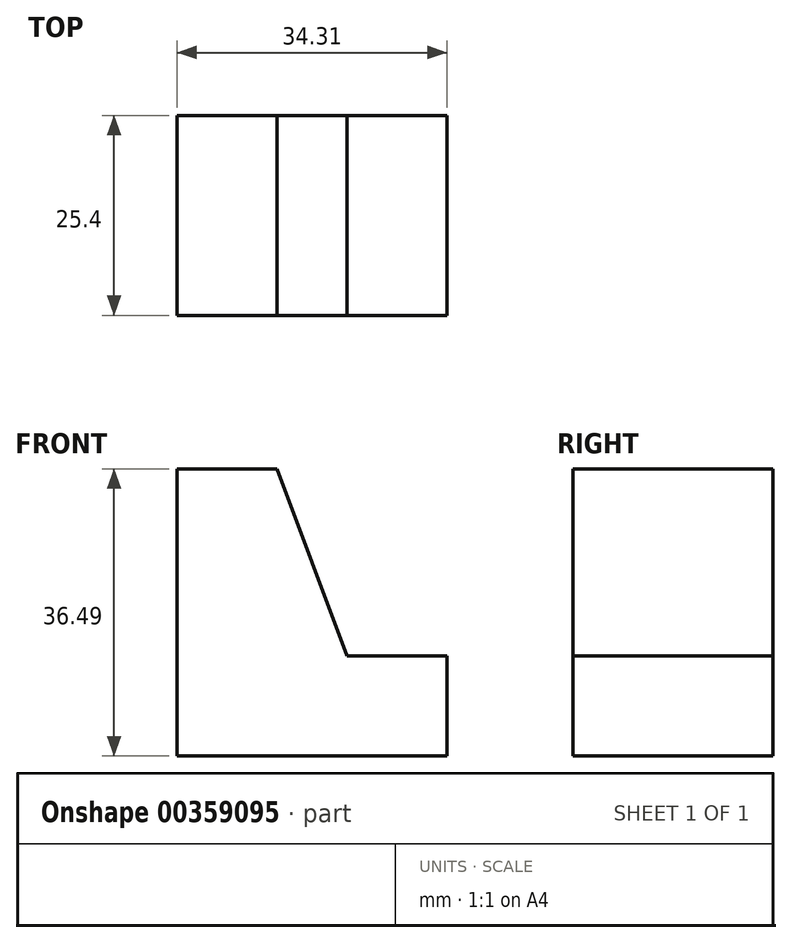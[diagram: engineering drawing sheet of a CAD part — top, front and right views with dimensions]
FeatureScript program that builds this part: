
annotation { "Feature Type Name" : "Feature", "Feature Type Description" : "" }
export const myFeature = defineFeature(function(context is Context, id is Id, definition is map)
    precondition{}
    {
        {
            var Q0;
            Q0=qCreatedBy(makeId("Front.planeOp"),FACE);
            var sketch = newSketch(context, id + "F0", { "sketchPlane" : qUnion([Q0])});
            skLineSegment(sketch, "E0", {"start": v(0, 0) * mm, "end": v(34.3, 0) * mm});
            skLineSegment(sketch, "E1", {"start": v(34.3, 0) * mm, "end": v(34.3, 12.7) * mm});
            skLineSegment(sketch, "E2", {"start": v(12.7, 36.49) * mm, "end": v(0, 36.49) * mm});
            skLineSegment(sketch, "E3", {"start": v(0, 36.49) * mm, "end": v(0, 0) * mm});
            skLineSegment(sketch, "E4", {"start": v(34.3, 12.7) * mm, "end": v(21.6, 12.7) * mm});
            skLineSegment(sketch, "E5", {"start": v(21.6, 12.7) * mm, "end": v(12.7, 36.49) * mm});
            skSolve(sketch);
        }
        {
            var Q0;
            Q0=makeQuery(id+"F0.imprint","IMPRINT",FACE,{"disambiguationData":[TD([[makeQuery(id+"F0.imprint","IMPRINT",EDGE,{"derivedFrom":sQuery(id+"F0.wireOp",EDGE,"E0")}),1.0]])]});
            extrude(context, id + "F1", {"entities" : qUnion([Q0]), "depth" : 25.4 * mm});
        }
    });
